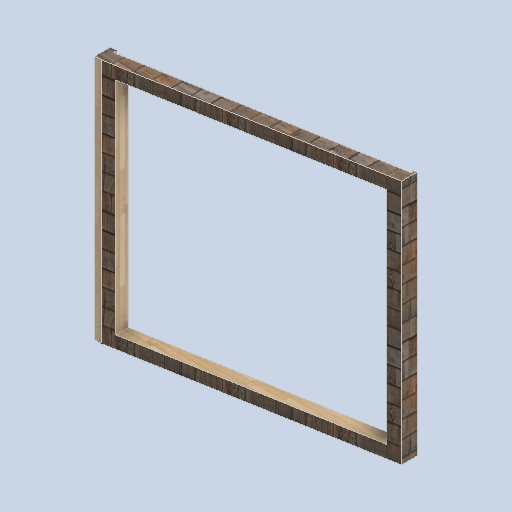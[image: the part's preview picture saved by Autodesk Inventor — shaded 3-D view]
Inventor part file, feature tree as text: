
AUTODESK INVENTOR PART (.ipt)
format: ipt  version: 2024.2 (Build 282272000, 272)  size: 404,992 bytes
history: native  units: mm
features: sketch x7, plane x4, extrude x3, projected_geometry x2, loft x1, other x1
ambient origin geometry x8: Origin, YZ Plane, XZ Plane, XY Plane, X Axis, Y Axis, Z Axis, Center Point
bodies: Solid1 (feature_tree)
feature tree (18):
  sketch  "Sketch1"  dims[d0=0.0mm d1=2500.0mm d2=150.0mm]
  plane  "Work Plane2"
  extrude  "Extrusion1"  Depth=150.0mm
  plane  "Work Plane3"
  sketch  "Sketch3"  dims[d3=60.0mm d4=0.0mm d5=0.0mm]
  sketch  "Sketch5"  dims[d6=13.962634mm d7=13.962634mm]
  plane  "Work Plane4"
  sketch  "Sketch6"  dims[d12=0.0mm d13=90.0deg d14=0.0mm d15=90.0deg]
  loft  "Loft2"
  extrude  "Extrusion2"  Depth=13.962634mm
  extrude  "Extrusion3"  TaperAngle=0.0deg  [1 undecoded]
  plane  "Work Plane1"
  projected_geometry  "Projected Loop1"
  sketch  "Sketch9"  dims[d16=30.0mm]
  other  "Edges2"
  sketch  "Sketch10"  dims[d17=2450.0mm]
  sketch  "Sketch11"  dims[d18=1.745329mm d19=2450.0mm d20=0.0mm d21=0.0mm d22=120.0mm d23=120.0mm d24=120.0mm d25=120.0mm d26=0.0mm d27=0.0mm]
  projected_geometry  "Projected Loop2"
note: 1 required parameter value undecoded (feature->parameter linkage not recoverable at this tier; creation-order binding heuristic only, values carry confidence <= 0.55)
